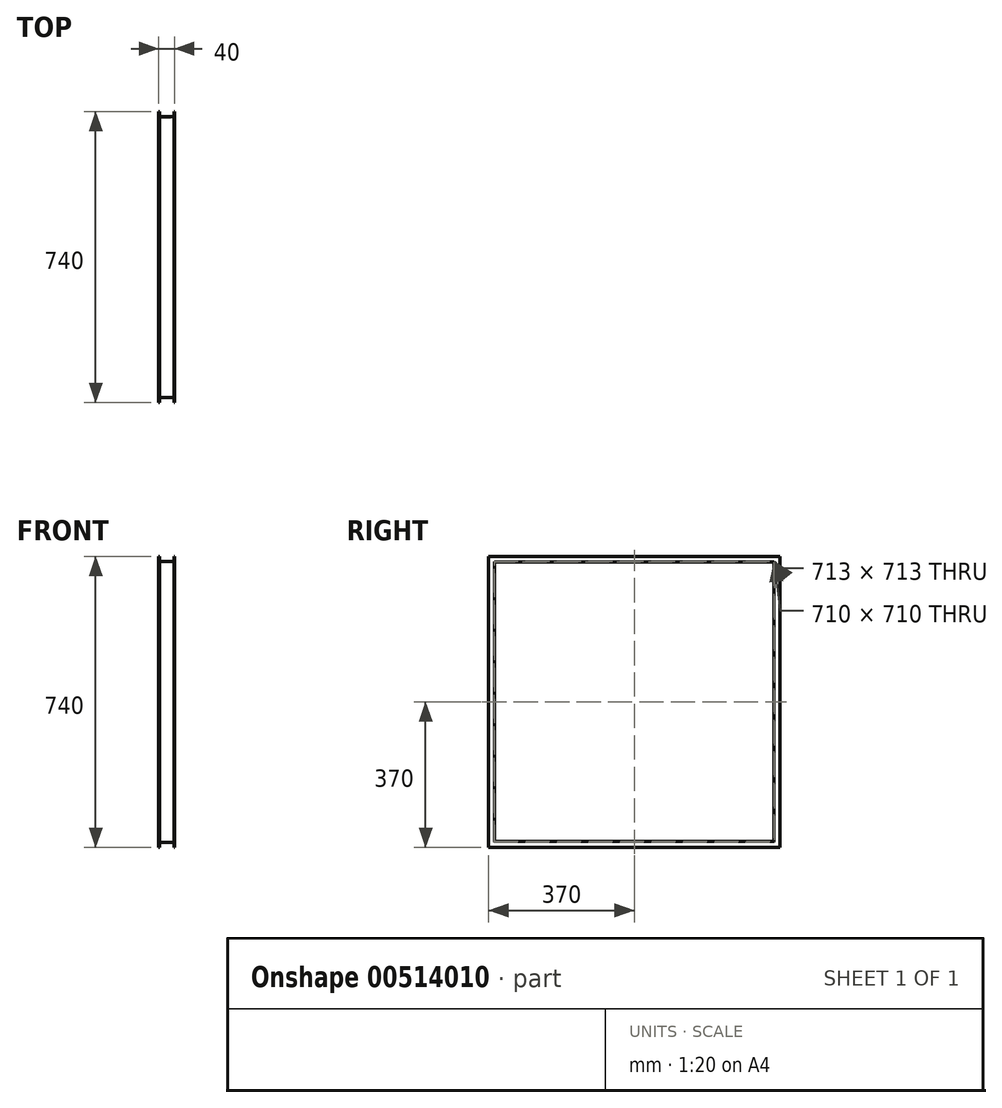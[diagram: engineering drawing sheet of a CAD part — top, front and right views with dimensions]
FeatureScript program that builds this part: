
annotation { "Feature Type Name" : "Feature", "Feature Type Description" : "" }
export const myFeature = defineFeature(function(context is Context, id is Id, definition is map)
    precondition{}
    {
        {
            var Q0;
            Q0=qCreatedBy(makeId("Top.planeOp"),FACE);
            var sketch = newSketch(context, id + "F0", { "sketchPlane" : qUnion([Q0])});
            skLineSegment(sketch, "E0.bottom", {"start": v(0, 0) * mm, "end": v(-40, 0) * mm});
            skLineSegment(sketch, "E0.top", {"start": v(0, -15) * mm, "end": v(-1.5, -15) * mm});
            skLineSegment(sketch, "E0.left", {"start": v(0, 0) * mm, "end": v(0, -15) * mm});
            skLineSegment(sketch, "E0.right", {"start": v(-40, 0) * mm, "end": v(-40, -15) * mm});
            skLineSegment(sketch, "E1.0", {"start": v(-38.5, -1.5) * mm, "end": v(-38.5, -15) * mm});
            skLineSegment(sketch, "E1.1", {"start": v(-1.5, -1.5) * mm, "end": v(-38.5, -1.5) * mm});
            skLineSegment(sketch, "E1.2", {"start": v(-1.5, -1.5) * mm, "end": v(-1.5, -15) * mm});
            skLineSegment(sketch, "E2.trimOffspring", {"start": v(-38.5, -15) * mm, "end": v(-40, -15) * mm});
            skSolve(sketch);
        }
        {
            var Q0;
            Q0=qCreatedBy(makeId("Right.planeOp"),FACE);
            var sketch = newSketch(context, id + "F1", { "sketchPlane" : qUnion([Q0])});
            skLineSegment(sketch, "E3", {"start": v(0, 0) * mm, "end": v(0, 710) * mm});
            skLineSegment(sketch, "E4", {"start": v(0, 710) * mm, "end": v(710, 710) * mm});
            skLineSegment(sketch, "E5", {"start": v(710, 710) * mm, "end": v(710, 0) * mm});
            skLineSegment(sketch, "E6", {"start": v(710, 0) * mm, "end": v(0, 0) * mm});
            skSolve(sketch);
        }
        {
            var Q0;
            Q0 = qSketchRegion(id + "F0", true);
            var Q1;
            Q1=sQuery(id+"F1.wireOp",EDGE,"E3");
            var Q2;
            Q2=sQuery(id+"F1.wireOp",EDGE,"E4");
            var Q3;
            Q3=sQuery(id+"F1.wireOp",EDGE,"E5");
            var Q4;
            Q4=sQuery(id+"F1.wireOp",EDGE,"E6");
            sweep(context, id + "F2", {"profiles" : qUnion([Q0]), "path" : qUnion([Q1, Q2, Q3, Q4])});
        }
    });
